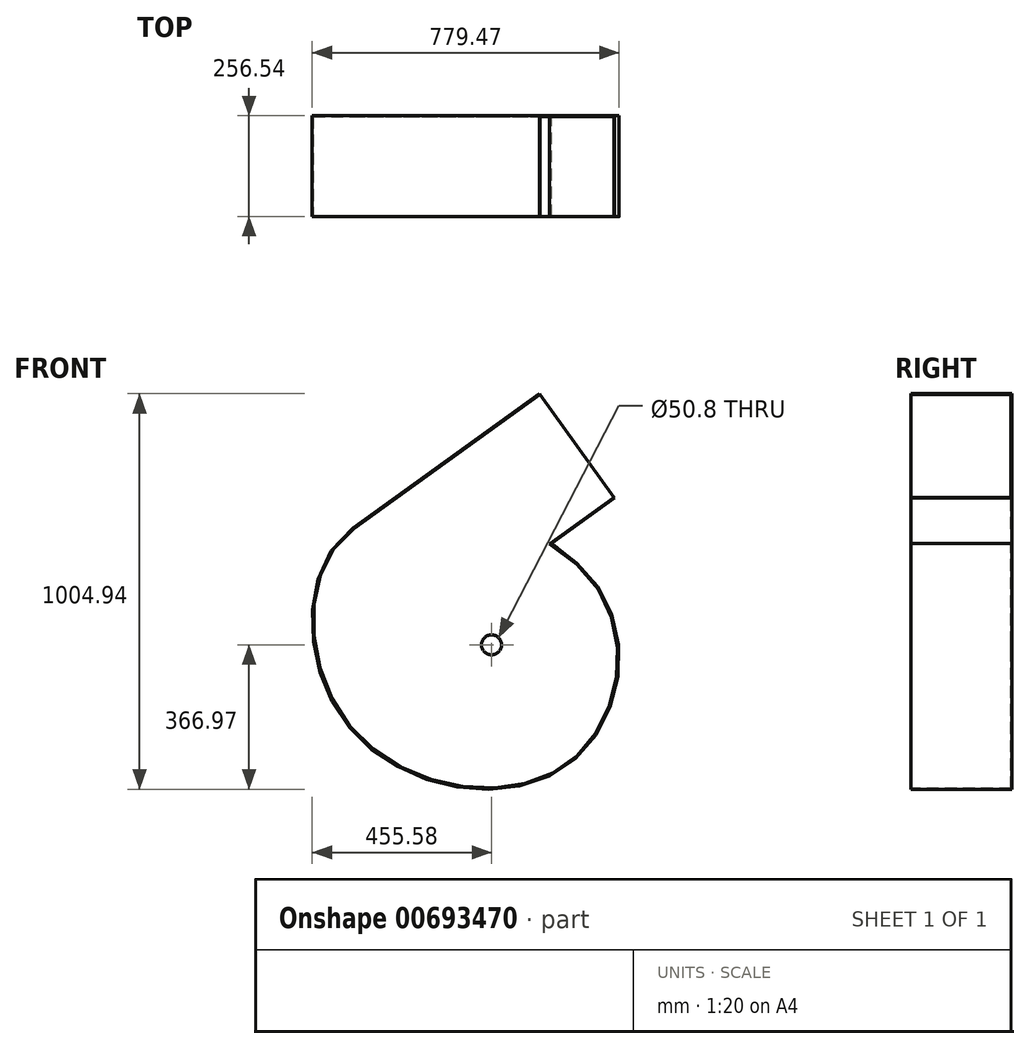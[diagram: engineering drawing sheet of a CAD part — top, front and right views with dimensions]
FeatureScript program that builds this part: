
annotation { "Feature Type Name" : "Feature", "Feature Type Description" : "" }
export const myFeature = defineFeature(function(context is Context, id is Id, definition is map)
    precondition{}
    {
        {
            var Q0;
            Q0=qCreatedBy(makeId("Front.planeOp"),FACE);
            var sketch = newSketch(context, id + "F0", { "sketchPlane" : qUnion([Q0])});
            skLineSegment(sketch, "E0", {"start": v(0, 0) * mm, "end": v(263.46, 152.1) * mm, "construction": true});
            skLineSegment(sketch, "E1", {"start": v(0, 0) * mm, "end": v(-350.8, 294.36) * mm, "construction": true});
            skLineSegment(sketch, "E2", {"start": v(0, 0) * mm, "end": v(179.78, -311.4) * mm, "construction": true});
            skLineSegment(sketch, "E3", {"start": v(0, 0) * mm, "end": v(-359.21, -207.4) * mm, "construction": true});
            skLineSegment(sketch, "E4", {"start": v(0, 0) * mm, "end": v(0, 464.04) * mm, "construction": true});
            skFitSpline(sketch, "E5", {"points": [v(-350.8, 294.36) * mm, v(-359.21, -207.4) * mm, v(179.78, -311.4) * mm, v(263.46, 152.1) * mm, v(-350.8, 294.36) * mm]});
            skLineSegment(sketch, "E6", {"start": v(-350.8, 294.36) * mm, "end": v(123.15, 635.9) * mm});
            skLineSegment(sketch, "E7", {"start": v(123.15, 635.9) * mm, "end": v(311.22, 374.94) * mm});
            skLineSegment(sketch, "E8", {"start": v(311.22, 374.94) * mm, "end": v(147.37, 256.87) * mm});
            skSolve(sketch);
        }
        {
            var Q0;
            Q0 = qSketchRegion(id + "F0", true);
            extrude(context, id + "F1", {"entities" : qUnion([Q0]), "depth" : 254 * mm, "offsetDistance" : 25.4 * mm});
        }
        {
            var Q0;
            Q0=makeQuery(id+"F1.opExtrude","CAP_FACE",FACE,{"disambiguationData":[OSD([sQuery(id+"F0.wireOp",EDGE,"E5"),sQuery(id+"F0.wireOp",EDGE,"E6"),sQuery(id+"F0.wireOp",EDGE,"E7"),sQuery(id+"F0.wireOp",EDGE,"E8")])],"isStart":false});
            var Q1;
            Q1=makeQuery(id+"F1.opExtrude","SWEPT_FACE",FACE,{"disambiguationData":[OSD([sQuery(id+"F0.wireOp",EDGE,"E7")])]});
            shell(context, id + "F2", {"entities" : qUnion([Q0, Q1]), "thickness" : 2.54 * mm, "oppositeDirection" : true});
        }
        {
            var Q0;
            Q0=makeQuery(id+"F2.opShell","OFFSET_FACE",FACE,{"disambiguationData":[OSD([sQuery(id+"F0.wireOp",EDGE,"E5"),sQuery(id+"F0.wireOp",EDGE,"E6"),sQuery(id+"F0.wireOp",EDGE,"E7"),sQuery(id+"F0.wireOp",EDGE,"E8")])]});
            var sketch = newSketch(context, id + "F3", { "sketchPlane" : qUnion([Q0])});
            skCircle(sketch, "E9", {"center": v(0, 0) * mm, "radius": 25.4 * mm});
            skSolve(sketch);
        }
        {
            var Q0;
            Q0 = qSketchRegion(id + "F3", true);
            extrude(context, id + "F4", {"entities" : qUnion([Q0]), "operationType" : NewBodyOperationType.REMOVE, "endBound" : BoundingType.UP_TO_NEXT, "oppositeDirection" : true, "depth" : 25.4 * mm, "offsetDistance" : 25.4 * mm});
        }
    });
